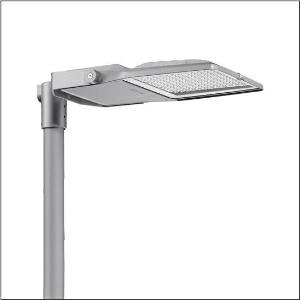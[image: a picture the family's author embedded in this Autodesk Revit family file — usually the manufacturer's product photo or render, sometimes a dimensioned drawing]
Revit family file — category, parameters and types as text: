
# Revit family: floodlight_fl_21_midi___pl52_5xa7785f2d3a_eb33
name_source: partatom
category: Lighting Fixtures
units: mm (PartAtom-declared; Revit-internal decimal feet)

## family parameters
Cut with Voids When Loaded = No
Host = Face
Light Source = No
Part Type = Normal
Room Calculation Point = No
Round Connector Dimension = Use Diameter
Shared = No

## types (1)
- --- (1 x LED, 35750 lm, 271.6 W, 3000K)
    Apparent Load = 272 VA
    CIE Flux Codes = 26 60 98 100 100
    Color Rendering = 70
    Color Temperature = 3000K
    Default Elevation = 1800 mm
    Description = Floodlight FL 21 midi, floodlight, primary light control with lens, of PMMA, primary optical cover: protective disc, of toughened safety glass, transparent, light distribution: PL52, light emission: direct distribution, installation type: surface-mounted, LED, High Power LED, rated luminous flux: 35.750lm, luminous efficacy: 132lm/W, light colour: 730, colour temperature: 3000K, control gear: ECG Smart Interface, control: flexible luminous flux parameterisation, time-dependent luminous flux control, constant luminous flux control, overheat protection, presetting dimming logarithmic, with terminal, 6-pole, mains connection: 220..240V, AC, 50/60Hz, start of lifetime: 272W, end of service life: 287W, reduction: 123W, luminaire housing, of diecast aluminium, powder-coated, Siteco® metallic grey (DB 702S), sealing non-destructively replaceable, please order mast flange separately, mast bracket, of steel, galvanised, powder-coated, Siteco® metallic grey (DB 702S), Smart Interface above, protection rating (complete): IP66, insulation class (complete): insulation class II (safety insulation), certification: CE, protection symbol: D, impact resistance: IK08, permissible operating ambient temperature: -40..+40°C, permissible operating ambient temperature for outdoor applications: -40..+50°C, standard: DIN EN 12944, LABS conformity tested according to VDMA 24364:2018-05, packaging unit: 1 piece

Light Distribution: PL52
    Height = 76 mm
    Lamp = 1 x LED
    Lamp Light Flux = 35750 lm
    Lamp Power = 271.6 W
    Lamp count = 1
    Length = 657 mm
    Luminous efficacy = 132 lm/W
    Manufacturer = Siteco
    ModVariant = No
    Model = 5XA7785F2D3A
    Number of Poles = 1
    OnlyDefault = Yes
    Power Factor = 1
    Product Name = Floodlight FL 21 midi | PL52
    Product group = floodlight | pylon annexe
    ProductGroupID = 6200
    Protection Class = Protection class II
    Protection Degree = IP 66
    RLX_Detail_Level = 1
    RLX_Emergency_Light_Flux = 0 lm
    RLX_Emergency_Type = 0
    RLX_Emergency_Type_DB = No
    RlxData = <blob elided: 153465 chars, md5=e60946db>
    Socket = socket
    Standby Power = 0 W
    System Light Flux = 35750 lm
    System Power = 272 W
    Type Comments = factory setting: luminous flux: 100 % | dim-lin: 254 | 620 mA
    Type Image = l_1007123.jpg
    URL = http://relux.com
    VarID = @adj_128663
    Voltage = 0 V
    Weight = 0.00 kg
    Width = 442 mm

## geometry (parser evidence)
native form markers: Blend x4, Sweep x14
no freeform markers — native parametric forms only
